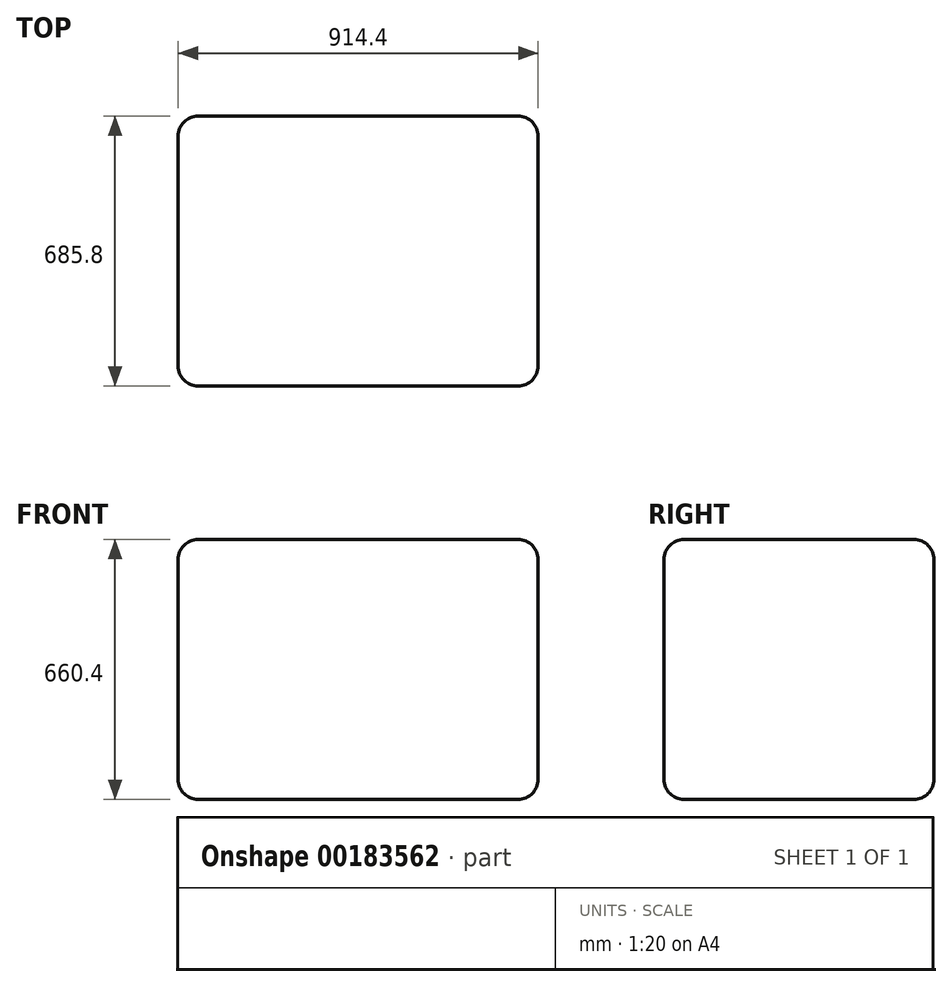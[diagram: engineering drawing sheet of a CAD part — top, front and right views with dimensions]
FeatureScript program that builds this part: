
annotation { "Feature Type Name" : "Feature", "Feature Type Description" : "" }
export const myFeature = defineFeature(function(context is Context, id is Id, definition is map)
    precondition{}
    {
        {
            var Q0;
            Q0=qCreatedBy(makeId("Right.planeOp"),FACE);
            var sketch = newSketch(context, id + "F0", { "sketchPlane" : qUnion([Q0])});
            skLineSegment(sketch, "E0.bottom", {"start": v(342.9, 330.2) * mm, "end": v(-342.9, 330.2) * mm});
            skLineSegment(sketch, "E0.top", {"start": v(342.9, -330.2) * mm, "end": v(-342.9, -330.2) * mm});
            skLineSegment(sketch, "E0.left", {"start": v(342.9, 330.2) * mm, "end": v(342.9, -330.2) * mm});
            skLineSegment(sketch, "E0.right", {"start": v(-342.9, 330.2) * mm, "end": v(-342.9, -330.2) * mm});
            skPoint(sketch, "E0.middle", {"position": v(0, 0) * mm});
            skSolve(sketch);
        }
        {
            var Q0;
            Q0=makeQuery(id+"F0.imprint","IMPRINT",FACE,{"disambiguationData":[TD([[makeQuery(id+"F0.imprint","IMPRINT",EDGE,{"derivedFrom":sQuery(id+"F0.wireOp",EDGE,"E0.bottom")}),1.0]])]});
            extrude(context, id + "F1", {"entities" : qUnion([Q0]), "depth" : 914.4 * mm});
        }
        {
            var Q0;
            Q0=makeQuery(id+"F1.opExtrude","CAP_EDGE",EDGE,{"disambiguationData":[OSD([sQuery(id+"F0.wireOp",EDGE,"E0.bottom")])],"isStart":true});
            var Q1;
            Q1=makeQuery(id+"F1.opExtrude","SWEPT_EDGE",EDGE,{"disambiguationData":[OSD([sQuery(id+"F0.wireOp",EDGE,"E0.bottom"),sQuery(id+"F0.wireOp",EDGE,"E0.left")])]});
            var Q2;
            Q2=makeQuery(id+"F1.opExtrude","SWEPT_FACE",FACE,{"disambiguationData":[OSD([sQuery(id+"F0.wireOp",EDGE,"E0.left")])]});
            var Q3;
            Q3=makeQuery(id+"F1.opExtrude","CAP_FACE",FACE,{"disambiguationData":[OSD([sQuery(id+"F0.wireOp",EDGE,"E0.bottom"),sQuery(id+"F0.wireOp",EDGE,"E0.top"),sQuery(id+"F0.wireOp",EDGE,"E0.left"),sQuery(id+"F0.wireOp",EDGE,"E0.right")])],"isStart":true});
            var Q4;
            Q4=makeQuery(id+"F1.opExtrude","SWEPT_FACE",FACE,{"disambiguationData":[OSD([sQuery(id+"F0.wireOp",EDGE,"E0.bottom")])]});
            var Q5;
            Q5=makeQuery(id+"F1.opExtrude","SWEPT_FACE",FACE,{"disambiguationData":[OSD([sQuery(id+"F0.wireOp",EDGE,"E0.right")])]});
            var Q6;
            Q6=makeQuery(id+"F1.opExtrude","CAP_FACE",FACE,{"disambiguationData":[OSD([sQuery(id+"F0.wireOp",EDGE,"E0.bottom"),sQuery(id+"F0.wireOp",EDGE,"E0.top"),sQuery(id+"F0.wireOp",EDGE,"E0.left"),sQuery(id+"F0.wireOp",EDGE,"E0.right")])],"isStart":false});
            var Q7;
            Q7=makeQuery(id+"F1.opExtrude","SWEPT_FACE",FACE,{"disambiguationData":[OSD([sQuery(id+"F0.wireOp",EDGE,"E0.top")])]});
            fillet(context, id + "F2", {"entities" : qUnion([Q0, Q1, Q2, Q3, Q4, Q5, Q6, Q7]), "radius" : 50.8 * mm, "tangentPropagation" : true, "allowEdgeOverflow" : false});
        }
    });
